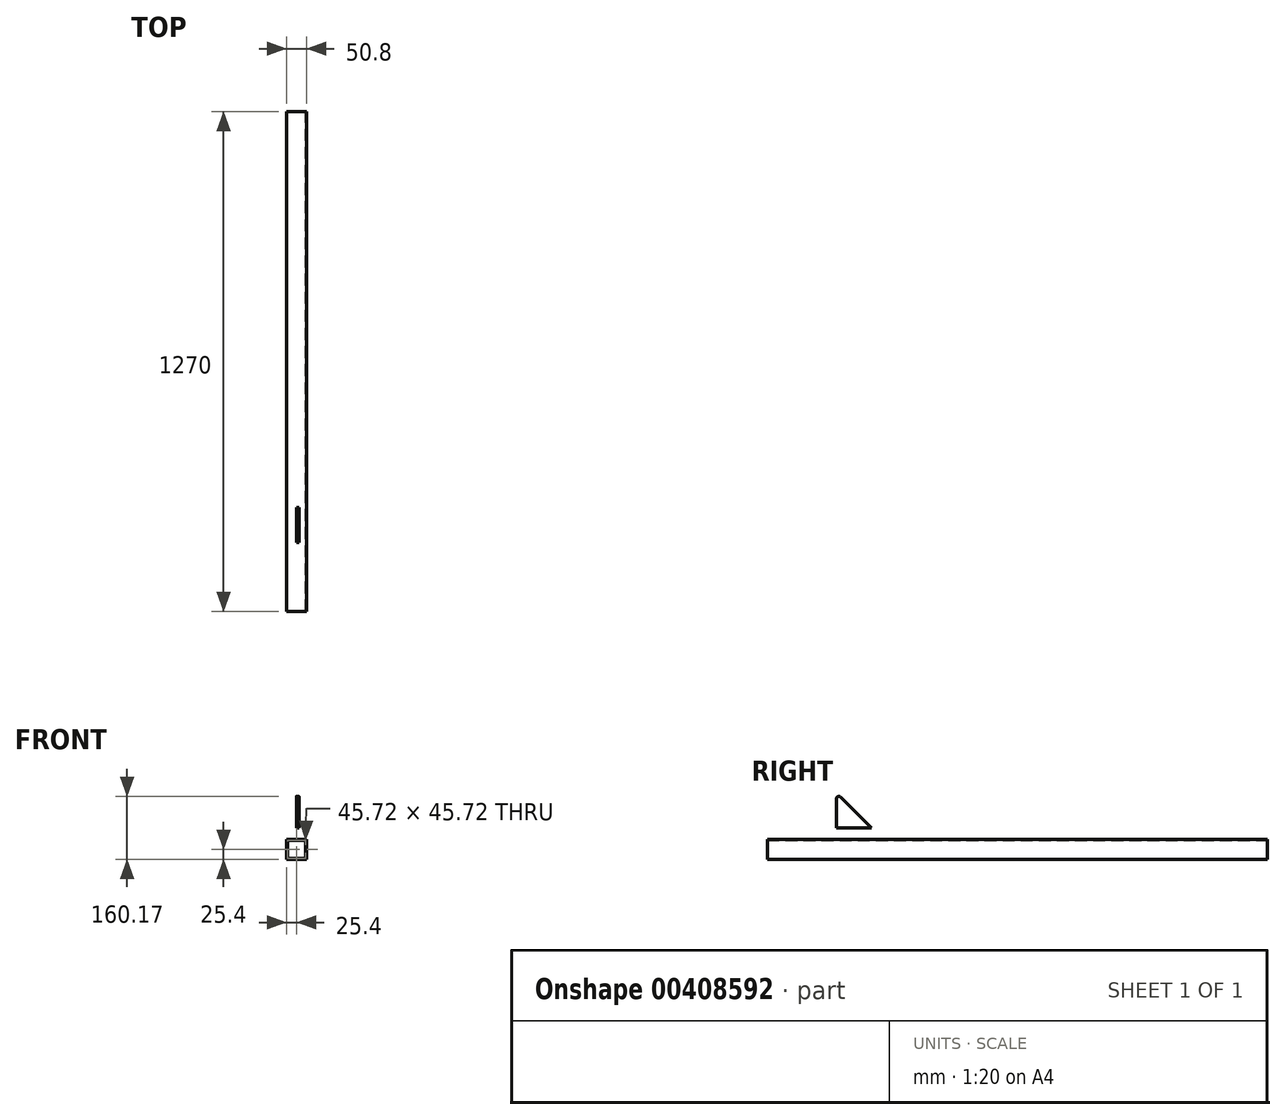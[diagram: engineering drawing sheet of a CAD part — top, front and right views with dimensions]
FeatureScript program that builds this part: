
annotation { "Feature Type Name" : "Feature", "Feature Type Description" : "" }
export const myFeature = defineFeature(function(context is Context, id is Id, definition is map)
    precondition{}
    {
        {
            var Q0;
            Q0=qCreatedBy(makeId("Front.planeOp"),FACE);
            var sketch = newSketch(context, id + "F0", { "sketchPlane" : qUnion([Q0])});
            skLineSegment(sketch, "E0.bottom", {"start": v(25.4, -25.4) * mm, "end": v(-25.4, -25.4) * mm});
            skLineSegment(sketch, "E0.top", {"start": v(25.4, 25.4) * mm, "end": v(-25.4, 25.4) * mm});
            skLineSegment(sketch, "E0.left", {"start": v(25.4, -25.4) * mm, "end": v(25.4, 25.4) * mm});
            skLineSegment(sketch, "E0.right", {"start": v(-25.4, -25.4) * mm, "end": v(-25.4, 25.4) * mm});
            skPoint(sketch, "E0.middle", {"position": v(0, 0) * mm});
            skSolve(sketch);
        }
        {
            var Q0;
            Q0=makeQuery(id+"F0.imprint","IMPRINT",FACE,{"disambiguationData":[TD([[makeQuery(id+"F0.imprint","IMPRINT",EDGE,{"derivedFrom":sQuery(id+"F0.wireOp",EDGE,"E0.bottom")}),-1.0]])]});
            extrude(context, id + "F1", {"entities" : qUnion([Q0]), "endBound" : BoundingType.SYMMETRIC, "depth" : 1270 * mm});
        }
        {
            var Q0;
            Q0=makeQuery(id+"F1.opExtrude","CAP_FACE",FACE,{"disambiguationData":[OSD([sQuery(id+"F0.wireOp",EDGE,"E0.bottom"),sQuery(id+"F0.wireOp",EDGE,"E0.top"),sQuery(id+"F0.wireOp",EDGE,"E0.left"),sQuery(id+"F0.wireOp",EDGE,"E0.right")])],"isStart":false});
            var Q1;
            Q1=makeQuery(id+"F1.opExtrude","CAP_FACE",FACE,{"disambiguationData":[OSD([sQuery(id+"F0.wireOp",EDGE,"E0.bottom"),sQuery(id+"F0.wireOp",EDGE,"E0.top"),sQuery(id+"F0.wireOp",EDGE,"E0.left"),sQuery(id+"F0.wireOp",EDGE,"E0.right")])],"isStart":true});
            shell(context, id + "F2", {"entities" : qUnion([Q0, Q1]), "thickness" : 2.54 * mm});
        }
        {
            var Q0;
            Q0=qCreatedBy(makeId("Right.planeOp"),FACE);
            var sketch = newSketch(context, id + "F3", { "sketchPlane" : qUnion([Q0])});
            skLineSegment(sketch, "E1", {"start": v(-459.49, 128.42) * mm, "end": v(-459.49, 54.85) * mm});
            skLineSegment(sketch, "E2", {"start": v(-459.49, 54.85) * mm, "end": v(-370.59, 54.85) * mm});
            skLineSegment(sketch, "E3", {"start": v(-370.59, 54.85) * mm, "end": v(-448.65, 132.9) * mm});
            skPoint(sketch, "E4.visualSharp", {"position": v(-459.49, 143.75) * mm});
            skArc(sketch, "E4.filletArc", {"start": v(-448.65, 132.9) * mm, "mid": v(-455.57, 134.28) * mm, "end": v(-459.49, 128.42) * mm});
            skPoint(sketch, "E5.visualSharp", {"position": v(-370.59, 54.85) * mm});
            skPoint(sketch, "E6.visualSharp", {"position": v(-459.49, 54.85) * mm});
            skSolve(sketch);
        }
        {
            var Q0;
            Q0=makeQuery(id+"F3.imprint","IMPRINT",FACE,{"disambiguationData":[TD([[makeQuery(id+"F3.imprint","IMPRINT",EDGE,{"derivedFrom":sQuery(id+"F3.wireOp",EDGE,"E1")}),1.0]])]});
            extrude(context, id + "F4", {"entities" : qUnion([Q0]), "depth" : 6.35 * mm});
        }
    });
